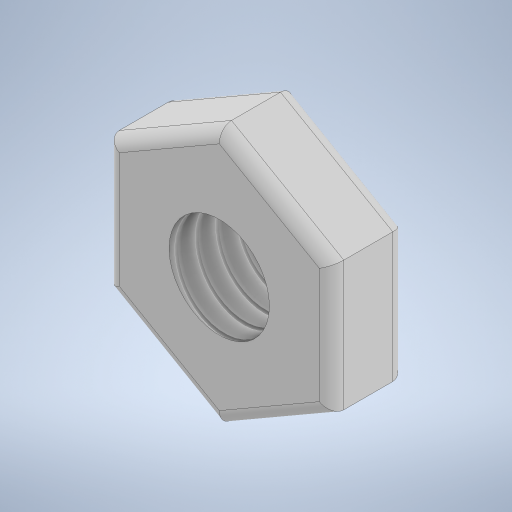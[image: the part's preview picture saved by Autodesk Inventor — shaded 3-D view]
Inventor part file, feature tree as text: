
AUTODESK INVENTOR PART (.ipt)
format: ipt  version: 2024 (Build 280153000, 153)  size: 250,368 bytes
history: native  units: in
note: dims shown in document units (in); Inventor stores cm internally (conversion verified against a paired STEP export)
features: extrude x1, thread x1, fillet x1, sketch x1
ambient origin geometry x8: Origin, YZ Plane, XZ Plane, XY Plane, X Axis, Y Axis, Z Axis, Center Point
bodies: Solid1 (feature_tree)
feature tree (4):
  extrude  "Extrusion1"  Depth=0.0118in
  thread  "Thread1"  [1 undecoded]
  fillet  "Fillet1"  Radius=0.0709in
  sketch  "Sketch1"  dims[d0=0.0968in d1=0.1811in d2=0.25in d3=0.0709in d4=0.0in d5=0.3937in d6=0.0in d7=0.0118in]
note: 1 required parameter value undecoded (feature->parameter linkage not recoverable at this tier; creation-order binding heuristic only, values carry confidence <= 0.55)
